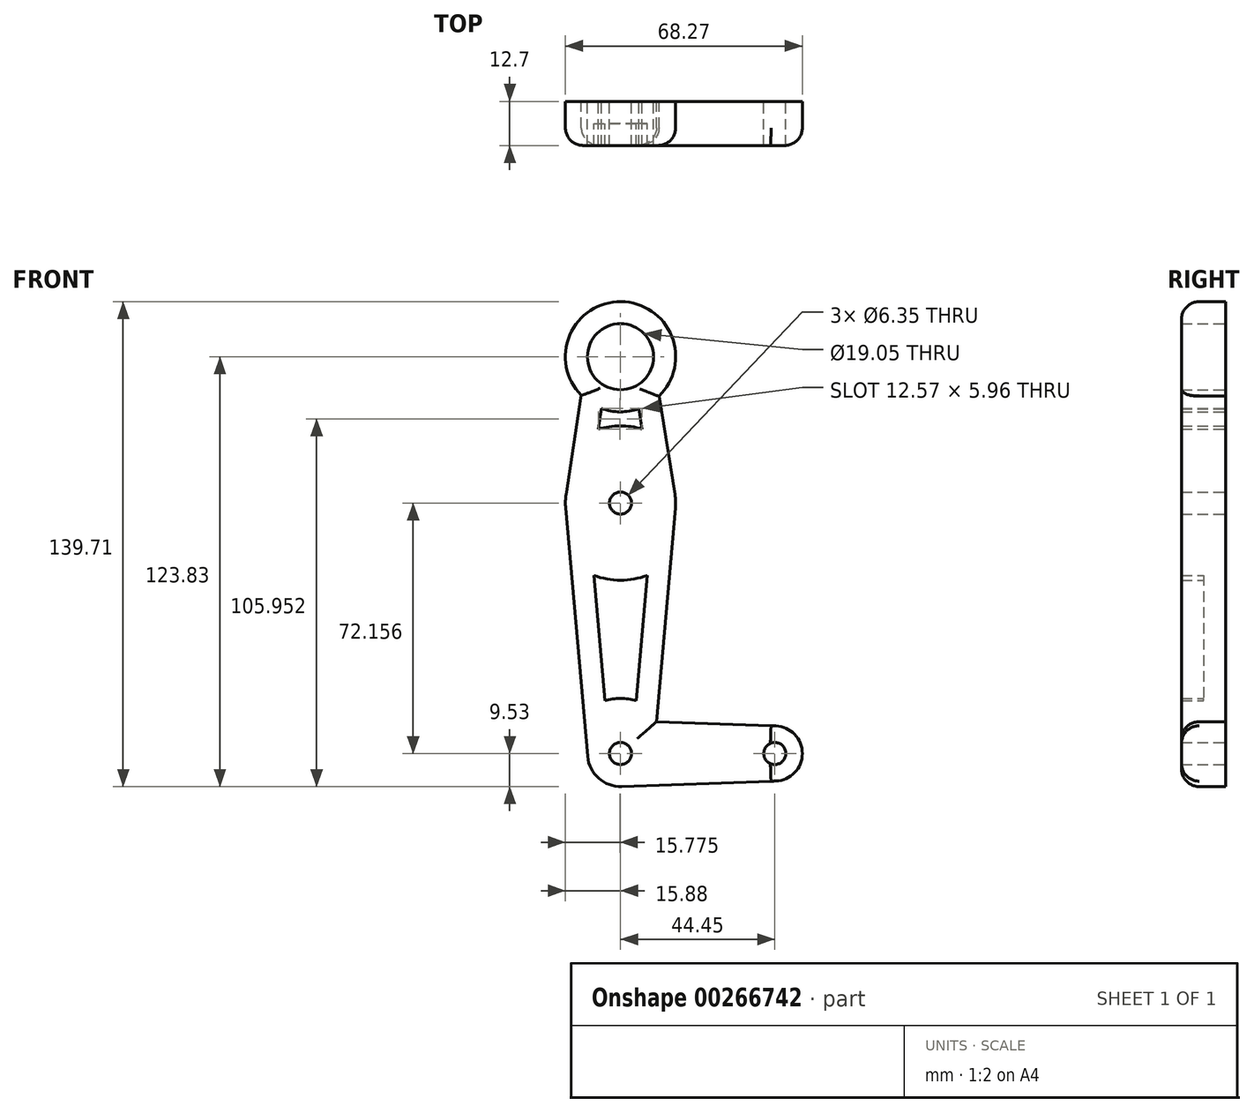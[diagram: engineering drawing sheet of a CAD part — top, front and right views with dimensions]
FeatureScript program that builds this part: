
annotation { "Feature Type Name" : "Feature", "Feature Type Description" : "" }
export const myFeature = defineFeature(function(context is Context, id is Id, definition is map)
    precondition{}
    {
        {
            var Q0;
            Q0=qCreatedBy(makeId("Front.planeOp"),FACE);
            var sketch = newSketch(context, id + "F0", { "sketchPlane" : qUnion([Q0])});
            skLineSegment(sketch, "E0", {"start": v(0, 0) * mm, "end": v(0, 114.3) * mm, "construction": true});
            skLineSegment(sketch, "E1", {"start": v(0, 0) * mm, "end": v(44.45, 0) * mm, "construction": true});
            skCircle(sketch, "E2", {"center": v(44.45, 0) * mm, "radius": 7.94 * mm});
            skCircle(sketch, "E3", {"center": v(44.45, 0) * mm, "radius": 3.18 * mm});
            skCircle(sketch, "E4", {"center": v(0, 0) * mm, "radius": 9.53 * mm});
            skCircle(sketch, "E5", {"center": v(0, 72.16) * mm, "radius": 15.88 * mm});
            skCircle(sketch, "E6", {"center": v(0, 114.3) * mm, "radius": 9.53 * mm});
            skCircle(sketch, "E7", {"center": v(0, 114.3) * mm, "radius": 3.18 * mm});
            skCircle(sketch, "E8", {"center": v(0, 72.16) * mm, "radius": 3.18 * mm});
            skCircle(sketch, "E9", {"center": v(0, 0) * mm, "radius": 3.18 * mm});
            skLineSegment(sketch, "E10", {"start": v(9.44, 113.04) * mm, "end": v(15.67, 74.7) * mm});
            skLineSegment(sketch, "E11", {"start": v(-9.42, 115.74) * mm, "end": v(-15.7, 74.55) * mm});
            skLineSegment(sketch, "E12", {"start": v(-15.81, 70.76) * mm, "end": v(-9.49, -0.84) * mm});
            skLineSegment(sketch, "E13", {"start": v(15.81, 70.76) * mm, "end": v(9.49, -0.84) * mm});
            skLineSegment(sketch, "E14", {"start": v(44.73, -7.93) * mm, "end": v(0.34, -9.52) * mm});
            skLineSegment(sketch, "E15", {"start": v(10.37, 9.16) * mm, "end": v(44.73, 7.93) * mm});
            skArc(sketch, "E16.0", {"start": v(-5.48, 99.4) * mm, "mid": v(-0.13, 98.43) * mm, "end": v(5.24, 99.31) * mm});
            skLineSegment(sketch, "E17.0", {"start": v(-5.48, 99.4) * mm, "end": v(-6.4, 93.44) * mm});
            skLineSegment(sketch, "E18.0", {"start": v(5.24, 99.31) * mm, "end": v(6.18, 93.5) * mm});
            skArc(sketch, "E19.0", {"start": v(-7.72, 51.32) * mm, "mid": v(0, 49.93) * mm, "end": v(7.72, 51.32) * mm});
            skArc(sketch, "E20.trimOffspring", {"start": v(11.08, 102.93) * mm, "mid": v(0.17, 130.17) * mm, "end": v(-11.33, 103.18) * mm});
            skArc(sketch, "E21.trimOffspring", {"start": v(6.18, 93.5) * mm, "mid": v(-0.1, 94.38) * mm, "end": v(-6.4, 93.44) * mm});
            skLineSegment(sketch, "E22.trimOffspring", {"start": v(7.72, 51.32) * mm, "end": v(4.53, 15.21) * mm});
            skLineSegment(sketch, "E23.trimOffspring", {"start": v(-7.72, 51.32) * mm, "end": v(-4.53, 15.21) * mm});
            skArc(sketch, "E24.trimOffspring", {"start": v(4.53, 15.21) * mm, "mid": v(0, 15.87) * mm, "end": v(-4.53, 15.21) * mm});
            skLineSegment(sketch, "E25.trimOffspring", {"start": v(3.19, 0) * mm, "end": v(3.16, -0.28) * mm});
            skSolve(sketch);
        }
        {
            var Q0;
            Q0=makeQuery(id+"F0.imprint","IMPRINT",FACE,{"disambiguationData":[TD([[makeQuery(id+"F0.imprint","IMPRINT",EDGE,{"derivedFrom":sQuery(id+"F0.wireOp",EDGE,"E3")}),-1.0]])]});
            var Q1;
            {var subQ5=sQuery(id+"F0.wireOp",EDGE,"E20.trimOffspring");Q1=makeQuery(id+"F0.imprint","IMPRINT",FACE,{"disambiguationData":[TD([[makeQuery(id+"F0.imprint","IMPRINT",EDGE,{"derivedFrom":subQ5}),1.0]])]});}
            var Q2;
            {var subQ0=sQuery(id+"F0.wireOp",EDGE,"E14");Q2=makeQuery(id+"F0.imprint","IMPRINT",FACE,{"disambiguationData":[TD([[makeQuery(id+"F0.imprint","IMPRINT",EDGE,{"derivedFrom":subQ0}),-1.0]])]});}
            var Q3;
            Q3=makeQuery(id+"F0.imprint","IMPRINT",FACE,{"disambiguationData":[TD([[makeQuery(id+"F0.imprint","IMPRINT",EDGE,{"derivedFrom":sQuery(id+"F0.wireOp",EDGE,"E8")}),-1.0]])]});
            var Q4;
            {var subQ3=sQuery(id+"F0.wireOp",EDGE,"c6bb880a-3332-4c1b-83b1-9befc54d9b94.trimOffspring");Q4=makeQuery(id+"F0.imprint","IMPRINT",FACE,{"disambiguationData":[TD([[makeQuery(id+"F0.imprint","IMPRINT",EDGE,{"derivedFrom":subQ3}),1.0]])]});}
            var Q5;
            Q5=makeQuery(id+"F0.imprint","IMPRINT",FACE,{"disambiguationData":[TD([[makeQuery(id+"F0.imprint","IMPRINT",EDGE,{"derivedFrom":sQuery(id+"F0.wireOp",EDGE,"E16.0")}),1.0]])]});
            var Q6;
            Q6=makeQuery(id+"F0.imprint","IMPRINT",FACE,{"disambiguationData":[TD([[makeQuery(id+"F0.imprint","IMPRINT",EDGE,{"derivedFrom":sQuery(id+"F0.wireOp",EDGE,"E9")}),-1.0]])]});
            var Q7;
            {var subQ0=sQuery(id+"F0.wireOp",EDGE,"E12");Q7=makeQuery(id+"F0.imprint","IMPRINT",FACE,{"disambiguationData":[TD([[makeQuery(id+"F0.imprint","IMPRINT",EDGE,{"derivedFrom":subQ0}),1.0]])]});}
            extrude(context, id + "F1", {"entities" : qUnion([Q0, Q1, Q2, Q3, Q4, Q5, Q6, Q7]), "depth" : 12.7 * mm});
        }
        {
            var Q0;
            Q0=makeQuery(id+"F1.opExtrude","CAP_EDGE",EDGE,{"disambiguationData":[OSD([sQuery(id+"F0.wireOp",EDGE,"E10")])],"isStart":false});
            fillet(context, id + "F2", {"entities" : qUnion([Q0]), "radius" : 5.08 * mm, "tangentPropagation" : true, "allowEdgeOverflow" : false});
        }
        {
            var Q0;
            {var subQ0=sQuery(id+"F0.wireOp",EDGE,"E15");Q0=makeQuery(id+"F1.opExtrude","CAP_EDGE",EDGE,{"disambiguationData":[OSD([subQ0]),TDD([makeQuery(id+"F0.imprint","IMPRINT",EDGE,{"disambiguationData":[TD([[makeQuery(id+"F0.imprint","INTERSECT",VERTEX,{"derivedFrom":[sQuery(id+"F0.wireOp",EDGE,"E2"),subQ0]}),1.0]])],"derivedFrom":subQ0})])],"isStart":false});}
            var Q1;
            Q1=makeQuery(id+"F1.opExtrude","CAP_EDGE",EDGE,{"disambiguationData":[OSD([sQuery(id+"F0.wireOp",EDGE,"E14")])],"isStart":false});
            var Q2;
            Q2=makeQuery(id+"F1.opExtrude","CAP_EDGE",EDGE,{"disambiguationData":[OSD([sQuery(id+"F0.wireOp",EDGE,"E2")])],"isStart":false});
            var Q3;
            Q3=makeQuery(id+"F1.opExtrude","CAP_EDGE",EDGE,{"disambiguationData":[OSD([sQuery(id+"F0.wireOp",EDGE,"E20.trimOffspring")])],"isStart":false});
            fillet(context, id + "F3", {"entities" : qUnion([Q0, Q1, Q2, Q3]), "radius" : 5.08 * mm, "tangentPropagation" : true, "allowEdgeOverflow" : false});
        }
        {
            var Q0;
            Q0=makeQuery(id+"F0.imprint","IMPRINT",FACE,{"disambiguationData":[TD([[makeQuery(id+"F0.imprint","IMPRINT",EDGE,{"derivedFrom":sQuery(id+"F0.wireOp",EDGE,"E19.0")}),-1.0]])]});
            extrude(context, id + "F4", {"entities" : qUnion([Q0]), "operationType" : NewBodyOperationType.ADD, "depth" : 6.35 * mm});
        }
    });
